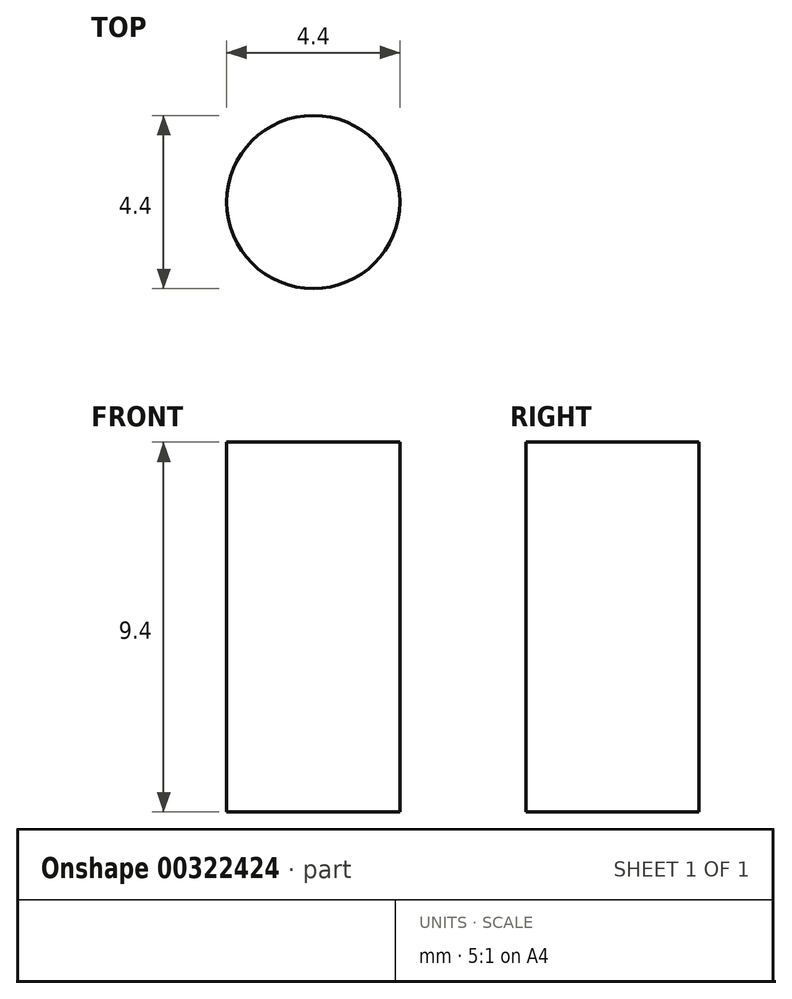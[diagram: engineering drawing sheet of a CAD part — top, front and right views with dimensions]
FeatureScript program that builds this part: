
annotation { "Feature Type Name" : "Feature", "Feature Type Description" : "" }
export const myFeature = defineFeature(function(context is Context, id is Id, definition is map)
    precondition{}
    {
        {
            var Q0;
            Q0=qCreatedBy(makeId("Top.planeOp"),FACE);
            var sketch = newSketch(context, id + "F0", { "sketchPlane" : qUnion([Q0])});
            skCircle(sketch, "E0", {"center": v(0, 0) * mm, "radius": 2.2 * mm});
            skSolve(sketch);
        }
        {
            var Q0;
            Q0 = qSketchRegion(id + "F0", true);
            extrude(context, id + "F1", {"entities" : qUnion([Q0]), "depth" : 9.4 * mm});
        }
    });
